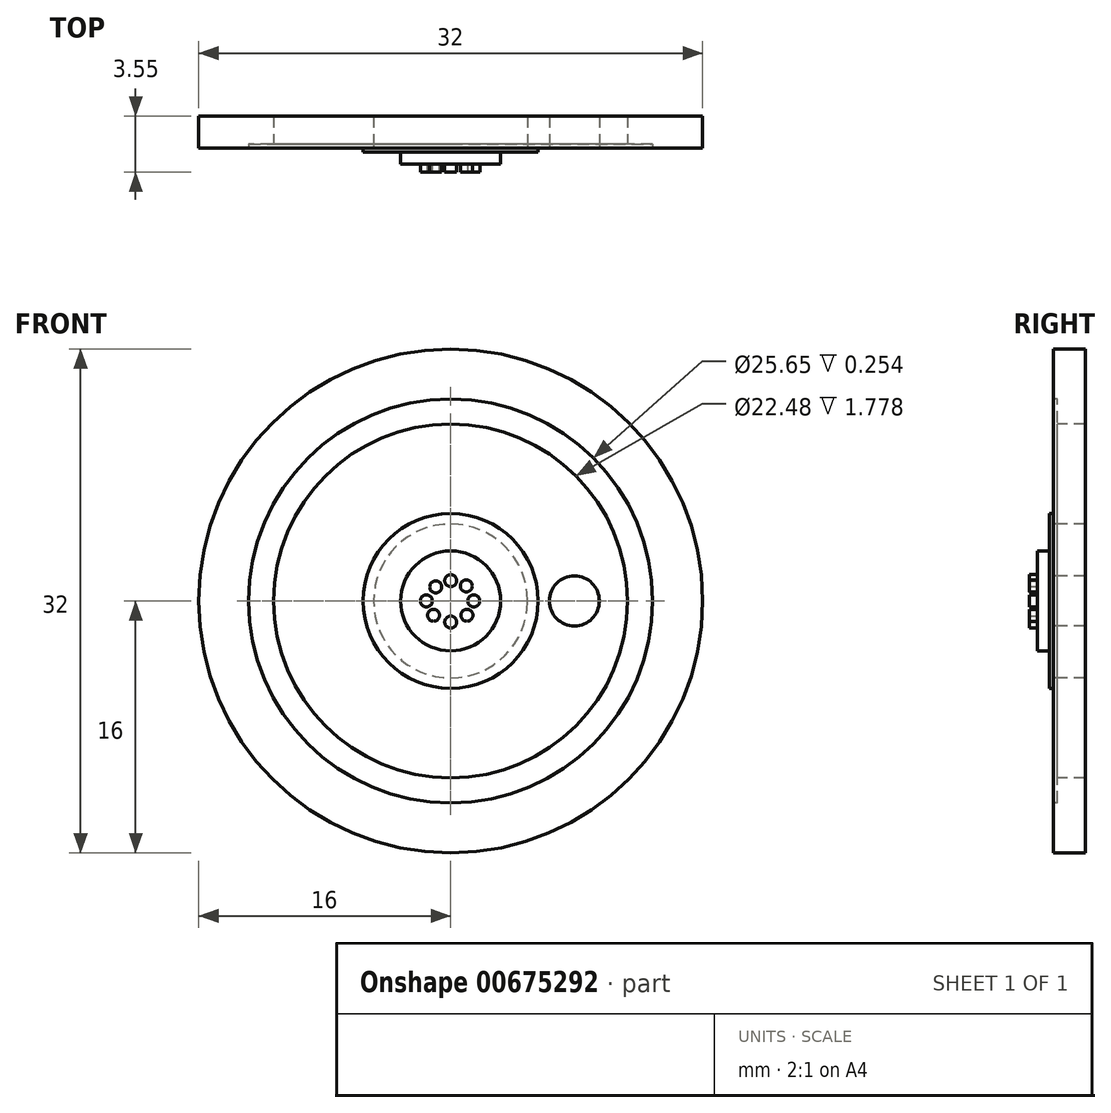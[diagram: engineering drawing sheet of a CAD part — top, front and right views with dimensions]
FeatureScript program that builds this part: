
annotation { "Feature Type Name" : "Feature", "Feature Type Description" : "" }
export const myFeature = defineFeature(function(context is Context, id is Id, definition is map)
    precondition{}
    {
        {
            var Q0;
            Q0=qCreatedBy(makeId("Front.planeOp"),FACE);
            var sketch = newSketch(context, id + "F0", { "sketchPlane" : qUnion([Q0])});
            skCircle(sketch, "E0", {"center": v(0, 0) * mm, "radius": 16 * mm});
            skSolve(sketch);
        }
        {
            var Q0;
            Q0=makeQuery(id+"F0.imprint","IMPRINT",FACE,{"disambiguationData":[TD([[makeQuery(id+"F0.imprint","IMPRINT",EDGE,{"derivedFrom":sQuery(id+"F0.wireOp",EDGE,"E0")}),1.0]])]});
            extrude(context, id + "F1", {"entities" : qUnion([Q0]), "oppositeDirection" : true, "depth" : 2.03 * mm, "offsetDistance" : 25.4 * mm});
        }
        {
            var Q0;
            Q0=makeQuery(id+"F1.opExtrude","CAP_FACE",FACE,{"disambiguationData":[OSD([sQuery(id+"F0.wireOp",EDGE,"E0")])],"isStart":true});
            var sketch = newSketch(context, id + "F2", { "sketchPlane" : qUnion([Q0])});
            skCircle(sketch, "E1", {"center": v(0, 0) * mm, "radius": 11.24 * mm});
            skCircle(sketch, "E2", {"center": v(0, 0) * mm, "radius": 4.89 * mm});
            skLineSegment(sketch, "E3", {"start": v(-11.24, 0) * mm, "end": v(11.24, 0) * mm});
            skCircle(sketch, "E4", {"center": v(-8.31, 0) * mm, "radius": 1.59 * mm});
            skCircle(sketch, "E5", {"center": v(7.86, 0) * mm, "radius": 1.59 * mm});
            skCircle(sketch, "E6", {"center": v(0, 7.92) * mm, "radius": 1.59 * mm});
            skCircle(sketch, "E7", {"center": v(0, -7.97) * mm, "radius": 1.59 * mm});
            skCircle(sketch, "E8", {"center": v(-5.86, -4.96) * mm, "radius": 1.59 * mm});
            skCircle(sketch, "E9", {"center": v(5.6, -5.31) * mm, "radius": 1.59 * mm});
            skCircle(sketch, "E10", {"center": v(-5.41, 5.4) * mm, "radius": 1.59 * mm});
            skCircle(sketch, "E11", {"center": v(5.37, 5.57) * mm, "radius": 1.59 * mm});
            skSolve(sketch);
        }
        {
            var Q0;
            Q0=makeQuery(id+"F1.opExtrude","CAP_FACE",FACE,{"disambiguationData":[OSD([sQuery(id+"F0.wireOp",EDGE,"E0")])],"isStart":true});
            var sketch = newSketch(context, id + "F3", { "sketchPlane" : qUnion([Q0])});
            skCircle(sketch, "E12", {"center": v(0, 0) * mm, "radius": 12.83 * mm});
            skCircle(sketch, "E13", {"center": v(0, 0) * mm, "radius": 11.23 * mm});
            skSolve(sketch);
        }
        {
            var Q0;
            Q0=makeQuery(id+"F3.imprint","IMPRINT",FACE,{"disambiguationData":[TD([[makeQuery(id+"F3.imprint","IMPRINT",EDGE,{"derivedFrom":sQuery(id+"F3.wireOp",EDGE,"E12")}),1.0]])]});
            extrude(context, id + "F4", {"entities" : qUnion([Q0]), "operationType" : NewBodyOperationType.REMOVE, "oppositeDirection" : true, "depth" : 0.25 * mm, "offsetDistance" : 25.4 * mm});
        }
        {
            var Q0;
            Q0=makeQuery(id+"F2.imprint","IMPRINT",FACE,{"disambiguationData":[TD([[makeQuery(id+"F2.imprint","IMPRINT",EDGE,{"derivedFrom":sQuery(id+"F2.wireOp",EDGE,"E7")}),1.0]])]});
            var Q1;
            Q1=makeQuery(id+"F2.imprint","IMPRINT",FACE,{"disambiguationData":[TD([[makeQuery(id+"F2.imprint","IMPRINT",EDGE,{"derivedFrom":sQuery(id+"F2.wireOp",EDGE,"E8")}),1.0]])]});
            var Q2;
            {var subQ0=sQuery(id+"F2.wireOp",EDGE,"E4");var subQ1=sQuery(id+"F2.wireOp",EDGE,"E3");var subQ2=makeQuery(id+"F2.imprint","INTERSECT",VERTEX,{"disambiguationData":[OD(0.0)],"derivedFrom":[subQ1,subQ0]});Q2=makeQuery(id+"F2.imprint","IMPRINT",FACE,{"disambiguationData":[TD([[makeQuery(id+"F2.imprint","IMPRINT",EDGE,{"disambiguationData":[TD([[subQ2,-1.0]])],"derivedFrom":subQ1}),-1.0]])]});}
            var Q3;
            {var subQ0=sQuery(id+"F2.wireOp",EDGE,"E4");var subQ1=sQuery(id+"F2.wireOp",EDGE,"E3");var subQ2=makeQuery(id+"F2.imprint","INTERSECT",VERTEX,{"disambiguationData":[OD(0.0)],"derivedFrom":[subQ1,subQ0]});Q3=makeQuery(id+"F2.imprint","IMPRINT",FACE,{"disambiguationData":[TD([[makeQuery(id+"F2.imprint","IMPRINT",EDGE,{"disambiguationData":[TD([[subQ2,-1.0]])],"derivedFrom":subQ1}),1.0]])]});}
            var Q4;
            Q4=makeQuery(id+"F2.imprint","IMPRINT",FACE,{"disambiguationData":[TD([[makeQuery(id+"F2.imprint","IMPRINT",EDGE,{"derivedFrom":sQuery(id+"F2.wireOp",EDGE,"E10")}),1.0]])]});
            var Q5;
            Q5=makeQuery(id+"F2.imprint","IMPRINT",FACE,{"disambiguationData":[TD([[makeQuery(id+"F2.imprint","IMPRINT",EDGE,{"derivedFrom":sQuery(id+"F2.wireOp",EDGE,"E6")}),1.0]])]});
            var Q6;
            Q6=makeQuery(id+"F2.imprint","IMPRINT",FACE,{"disambiguationData":[TD([[makeQuery(id+"F2.imprint","IMPRINT",EDGE,{"derivedFrom":sQuery(id+"F2.wireOp",EDGE,"E11")}),1.0]])]});
            var Q7;
            {var subQ0=sQuery(id+"F2.wireOp",EDGE,"E5");var subQ1=sQuery(id+"F2.wireOp",EDGE,"E3");var subQ2=makeQuery(id+"F2.imprint","INTERSECT",VERTEX,{"disambiguationData":[OD(0.0)],"derivedFrom":[subQ1,subQ0]});Q7=makeQuery(id+"F2.imprint","IMPRINT",FACE,{"disambiguationData":[TD([[makeQuery(id+"F2.imprint","IMPRINT",EDGE,{"disambiguationData":[TD([[subQ2,-1.0]])],"derivedFrom":subQ1}),1.0]])]});}
            var Q8;
            {var subQ0=sQuery(id+"F2.wireOp",EDGE,"E5");var subQ1=sQuery(id+"F2.wireOp",EDGE,"E3");var subQ2=makeQuery(id+"F2.imprint","INTERSECT",VERTEX,{"disambiguationData":[OD(0.0)],"derivedFrom":[subQ1,subQ0]});Q8=makeQuery(id+"F2.imprint","IMPRINT",FACE,{"disambiguationData":[TD([[makeQuery(id+"F2.imprint","IMPRINT",EDGE,{"disambiguationData":[TD([[subQ2,-1.0]])],"derivedFrom":subQ1}),-1.0]])]});}
            var Q9;
            Q9=makeQuery(id+"F2.imprint","IMPRINT",FACE,{"disambiguationData":[TD([[makeQuery(id+"F2.imprint","IMPRINT",EDGE,{"derivedFrom":sQuery(id+"F2.wireOp",EDGE,"E9")}),1.0]])]});
            extrude(context, id + "F5", {"entities" : qUnion([Q0, Q1, Q2, Q3, Q4, Q5, Q6, Q7, Q8, Q9]), "operationType" : NewBodyOperationType.REMOVE, "oppositeDirection" : true, "depth" : 2.03 * mm, "offsetDistance" : 25.4 * mm});
        }
        {
            var Q0;
            Q0=makeQuery(id+"F4.boolean.opBoolean","SPLIT",FACE,{"disambiguationData":[TD([makeQuery(id+"F4.opExtrude","SWEPT_FACE",FACE,{"disambiguationData":[OSD([sQuery(id+"F3.wireOp",EDGE,"E13")])]})])],"derivedFrom":makeQuery(id+"F1.opExtrude","CAP_FACE",FACE,{"disambiguationData":[OSD([sQuery(id+"F0.wireOp",EDGE,"E0")])],"isStart":true})});
            var sketch = newSketch(context, id + "F6", { "sketchPlane" : qUnion([Q0])});
            skCircle(sketch, "E14", {"center": v(0, 0) * mm, "radius": 5.56 * mm});
            skSolve(sketch);
        }
        {
            var Q0;
            Q0=makeQuery(id+"F6.imprint","IMPRINT",FACE,{"disambiguationData":[TD([[makeQuery(id+"F6.imprint","IMPRINT",EDGE,{"derivedFrom":sQuery(id+"F6.wireOp",EDGE,"E14")}),1.0]])]});
            extrude(context, id + "F7", {"entities" : qUnion([Q0]), "operationType" : NewBodyOperationType.ADD, "depth" : 0.25 * mm, "offsetDistance" : 25.4 * mm});
        }
        {
            var Q0;
            Q0=makeQuery(id+"F7.opExtrude","CAP_FACE",FACE,{"disambiguationData":[OSD([sQuery(id+"F6.wireOp",EDGE,"E14")])],"isStart":false});
            var sketch = newSketch(context, id + "F8", { "sketchPlane" : qUnion([Q0])});
            skCircle(sketch, "E15", {"center": v(0, 0) * mm, "radius": 3.17 * mm});
            skSolve(sketch);
        }
        {
            var Q0;
            Q0=makeQuery(id+"F8.imprint","IMPRINT",FACE,{"disambiguationData":[TD([[makeQuery(id+"F8.imprint","IMPRINT",EDGE,{"derivedFrom":sQuery(id+"F8.wireOp",EDGE,"E15")}),1.0]])]});
            extrude(context, id + "F9", {"entities" : qUnion([Q0]), "operationType" : NewBodyOperationType.ADD, "depth" : 0.76 * mm, "offsetDistance" : 25.4 * mm});
        }
        {
            var Q0;
            Q0=makeQuery(id+"F9.opExtrude","CAP_FACE",FACE,{"disambiguationData":[OSD([sQuery(id+"F8.wireOp",EDGE,"E15")])],"isStart":false});
            var sketch = newSketch(context, id + "F10", { "sketchPlane" : qUnion([Q0])});
            skCircle(sketch, "E16", {"center": v(0, 1.3) * mm, "radius": 0.38 * mm});
            skCircle(sketch, "E17", {"center": v(1.47, 0) * mm, "radius": 0.38 * mm});
            skCircle(sketch, "E18", {"center": v(0, -1.34) * mm, "radius": 0.38 * mm});
            skCircle(sketch, "E19", {"center": v(-1.54, 0) * mm, "radius": 0.38 * mm});
            skCircle(sketch, "E20", {"center": v(-0.95, 0.9) * mm, "radius": 0.38 * mm});
            skCircle(sketch, "E21", {"center": v(1, 0.96) * mm, "radius": 0.38 * mm});
            skCircle(sketch, "E22", {"center": v(1.03, -0.9) * mm, "radius": 0.38 * mm});
            skCircle(sketch, "E23", {"center": v(-1.09, -0.9) * mm, "radius": 0.38 * mm});
            skSolve(sketch);
        }
        {
            var Q0;
            Q0=makeQuery(id+"F10.imprint","IMPRINT",FACE,{"disambiguationData":[TD([[makeQuery(id+"F10.imprint","IMPRINT",EDGE,{"derivedFrom":sQuery(id+"F10.wireOp",EDGE,"E19")}),1.0]])]});
            var Q1;
            Q1=makeQuery(id+"F10.imprint","IMPRINT",FACE,{"disambiguationData":[TD([[makeQuery(id+"F10.imprint","IMPRINT",EDGE,{"derivedFrom":sQuery(id+"F10.wireOp",EDGE,"E20")}),1.0]])]});
            var Q2;
            Q2=makeQuery(id+"F10.imprint","IMPRINT",FACE,{"disambiguationData":[TD([[makeQuery(id+"F10.imprint","IMPRINT",EDGE,{"derivedFrom":sQuery(id+"F10.wireOp",EDGE,"E16")}),1.0]])]});
            var Q3;
            Q3=makeQuery(id+"F10.imprint","IMPRINT",FACE,{"disambiguationData":[TD([[makeQuery(id+"F10.imprint","IMPRINT",EDGE,{"derivedFrom":sQuery(id+"F10.wireOp",EDGE,"E21")}),1.0]])]});
            var Q4;
            Q4=makeQuery(id+"F10.imprint","IMPRINT",FACE,{"disambiguationData":[TD([[makeQuery(id+"F10.imprint","IMPRINT",EDGE,{"derivedFrom":sQuery(id+"F10.wireOp",EDGE,"E17")}),1.0]])]});
            var Q5;
            Q5=makeQuery(id+"F10.imprint","IMPRINT",FACE,{"disambiguationData":[TD([[makeQuery(id+"F10.imprint","IMPRINT",EDGE,{"derivedFrom":sQuery(id+"F10.wireOp",EDGE,"E22")}),1.0]])]});
            var Q6;
            Q6=makeQuery(id+"F10.imprint","IMPRINT",FACE,{"disambiguationData":[TD([[makeQuery(id+"F10.imprint","IMPRINT",EDGE,{"derivedFrom":sQuery(id+"F10.wireOp",EDGE,"E18")}),1.0]])]});
            var Q7;
            Q7=makeQuery(id+"F10.imprint","IMPRINT",FACE,{"disambiguationData":[TD([[makeQuery(id+"F10.imprint","IMPRINT",EDGE,{"derivedFrom":sQuery(id+"F10.wireOp",EDGE,"E23")}),1.0]])]});
            extrude(context, id + "F11", {"entities" : qUnion([Q0, Q1, Q2, Q3, Q4, Q5, Q6, Q7]), "operationType" : NewBodyOperationType.ADD, "depth" : 0.5 * mm, "offsetDistance" : 25.4 * mm});
        }
    });
